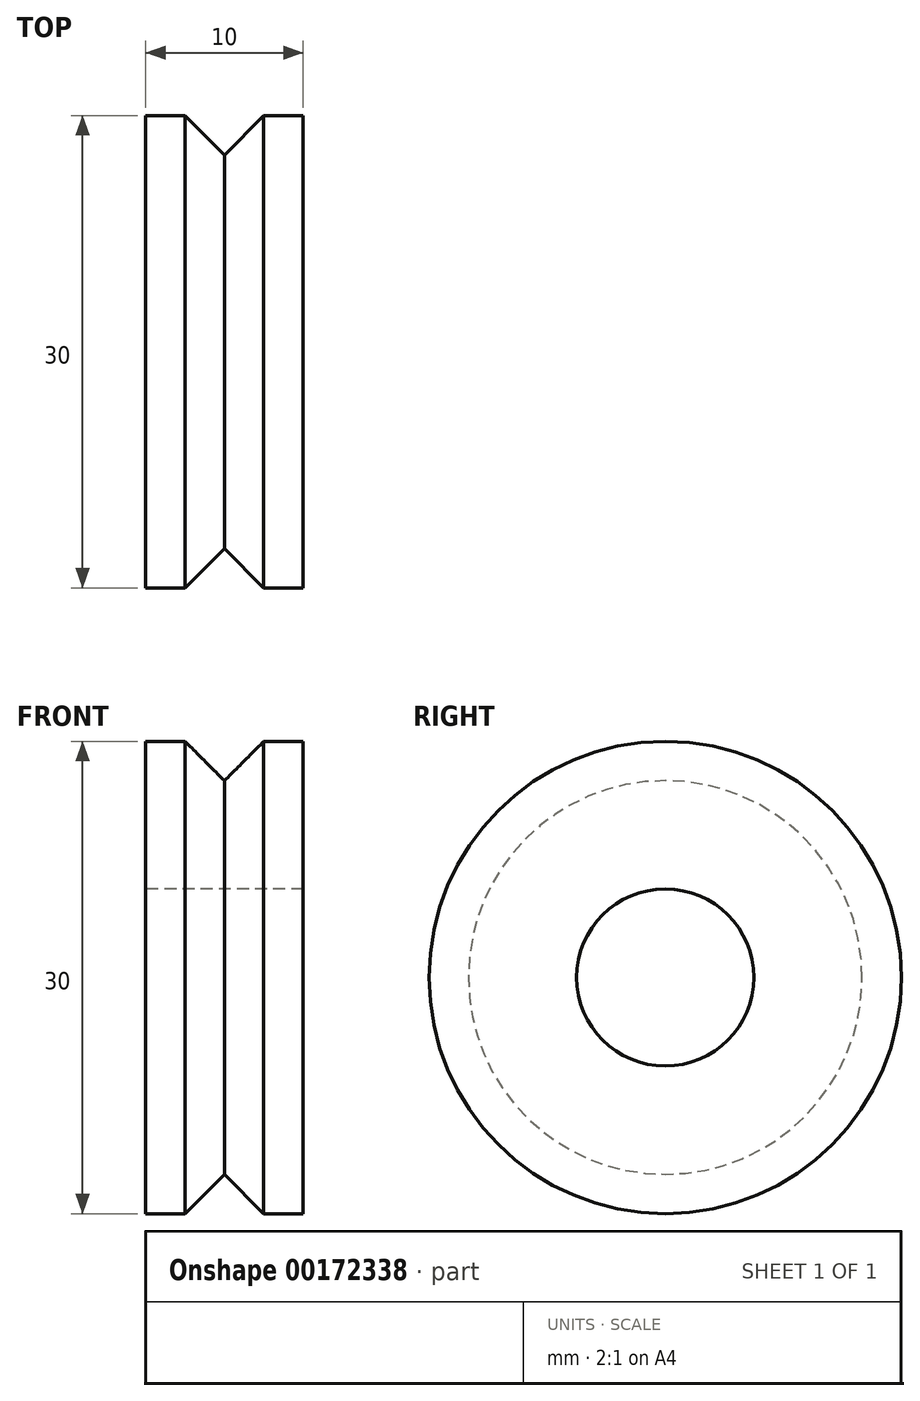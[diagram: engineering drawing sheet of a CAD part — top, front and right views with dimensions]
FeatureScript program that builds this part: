
annotation { "Feature Type Name" : "Feature", "Feature Type Description" : "" }
export const myFeature = defineFeature(function(context is Context, id is Id, definition is map)
    precondition{}
    {
        {
            var Q0;
            Q0=qCreatedBy(makeId("Front.planeOp"),FACE);
            var sketch = newSketch(context, id + "F0", { "sketchPlane" : qUnion([Q0])});
            skLineSegment(sketch, "E0", {"start": v(-4.33, 0) * mm, "end": v(-4.33, 5.63) * mm});
            skLineSegment(sketch, "E1", {"start": v(-4.33, 5.62) * mm, "end": v(5.67, 5.62) * mm});
            skLineSegment(sketch, "E2", {"start": v(5.67, 5.63) * mm, "end": v(5.67, 0) * mm});
            skLineSegment(sketch, "E3", {"start": v(-4.33, 5.63) * mm, "end": v(-4.33, 15) * mm});
            skLineSegment(sketch, "E4", {"start": v(5.67, 15) * mm, "end": v(5.67, 5.62) * mm});
            skLineSegment(sketch, "E5", {"start": v(-4.33, 15) * mm, "end": v(-1.83, 15) * mm});
            skLineSegment(sketch, "E6", {"start": v(-1.83, 15) * mm, "end": v(0.67, 12.5) * mm});
            skLineSegment(sketch, "E7", {"start": v(0.67, 12.5) * mm, "end": v(3.17, 15) * mm});
            skLineSegment(sketch, "E8", {"start": v(3.17, 15) * mm, "end": v(5.67, 15) * mm});
            skLineSegment(sketch, "E9", {"start": v(0.67, 21.16) * mm, "end": v(0.67, 0) * mm, "construction": true});
            skLineSegment(sketch, "E10", {"start": v(-11.04, 0) * mm, "end": v(14.62, 0) * mm, "construction": true});
            skSolve(sketch);
        }
        {
            var Q0;
            Q0 = qSketchRegion(id + "F0", true);
            var Q1;
            Q1=sQuery(id+"F0.wireOp",EDGE,"E10");
            revolve(context, id + "F1", {"entities" : qUnion([Q0]), "axis" : qUnion([Q1]), "revolveType" : RevolveType.FULL});
        }
    });
